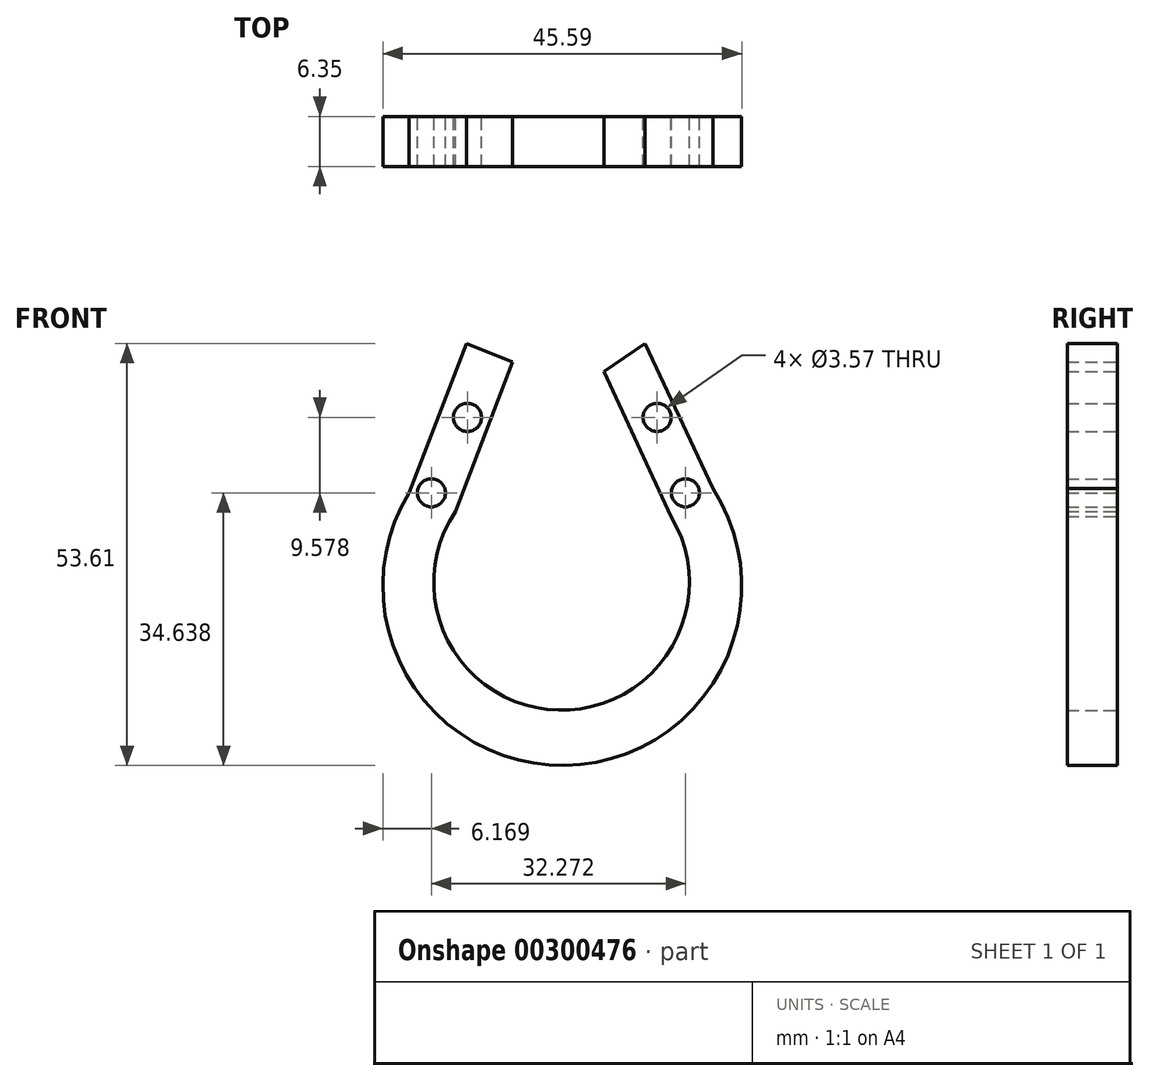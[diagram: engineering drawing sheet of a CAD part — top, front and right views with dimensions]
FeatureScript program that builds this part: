
annotation { "Feature Type Name" : "Feature", "Feature Type Description" : "" }
export const myFeature = defineFeature(function(context is Context, id is Id, definition is map)
    precondition{}
    {
        {
            var Q0;
            Q0=qCreatedBy(makeId("Front.planeOp"),FACE);
            var sketch = newSketch(context, id + "F0", { "sketchPlane" : qUnion([Q0])});
            skLineSegment(sketch, "E0", {"start": v(-45.03, 48.8) * mm, "end": v(-52.3, 29.83) * mm});
            skLineSegment(sketch, "E1", {"start": v(-22.3, 48.8) * mm, "end": v(-13.71, 30.39) * mm});
            skArc(sketch, "E2", {"start": v(-52.3, 29.83) * mm, "mid": v(-32.5, -4.8) * mm, "end": v(-13.71, 30.39) * mm});
            skLineSegment(sketch, "E3", {"start": v(-46.4, 27.47) * mm, "end": v(-39.13, 46.45) * mm});
            skLineSegment(sketch, "E4", {"start": v(-27.56, 45.23) * mm, "end": v(-19.01, 26.79) * mm});
            skLineSegment(sketch, "E5", {"start": v(-45.03, 48.8) * mm, "end": v(-39.13, 46.45) * mm});
            skLineSegment(sketch, "E6", {"start": v(-27.56, 45.23) * mm, "end": v(-22.3, 48.8) * mm});
            skArc(sketch, "E7", {"start": v(-46.4, 27.47) * mm, "mid": v(-33.33, 2.21) * mm, "end": v(-19.01, 26.79) * mm});
            skCircle(sketch, "E8", {"center": v(-44.88, 39.4) * mm, "radius": 1.78 * mm});
            skCircle(sketch, "E9", {"center": v(-20.79, 39.4) * mm, "radius": 1.78 * mm});
            skCircle(sketch, "E10", {"center": v(-49.46, 29.83) * mm, "radius": 1.78 * mm});
            skCircle(sketch, "E11", {"center": v(-17.19, 29.83) * mm, "radius": 1.78 * mm});
            skSolve(sketch);
        }
        {
            var Q0;
            Q0=makeQuery(id+"F0.imprint","IMPRINT",FACE,{"disambiguationData":[TD([[makeQuery(id+"F0.imprint","IMPRINT",EDGE,{"derivedFrom":sQuery(id+"F0.wireOp",EDGE,"E0")}),1.0]])]});
            extrude(context, id + "F1", {"entities" : qUnion([Q0]), "depth" : 6.35 * mm});
        }
    });
